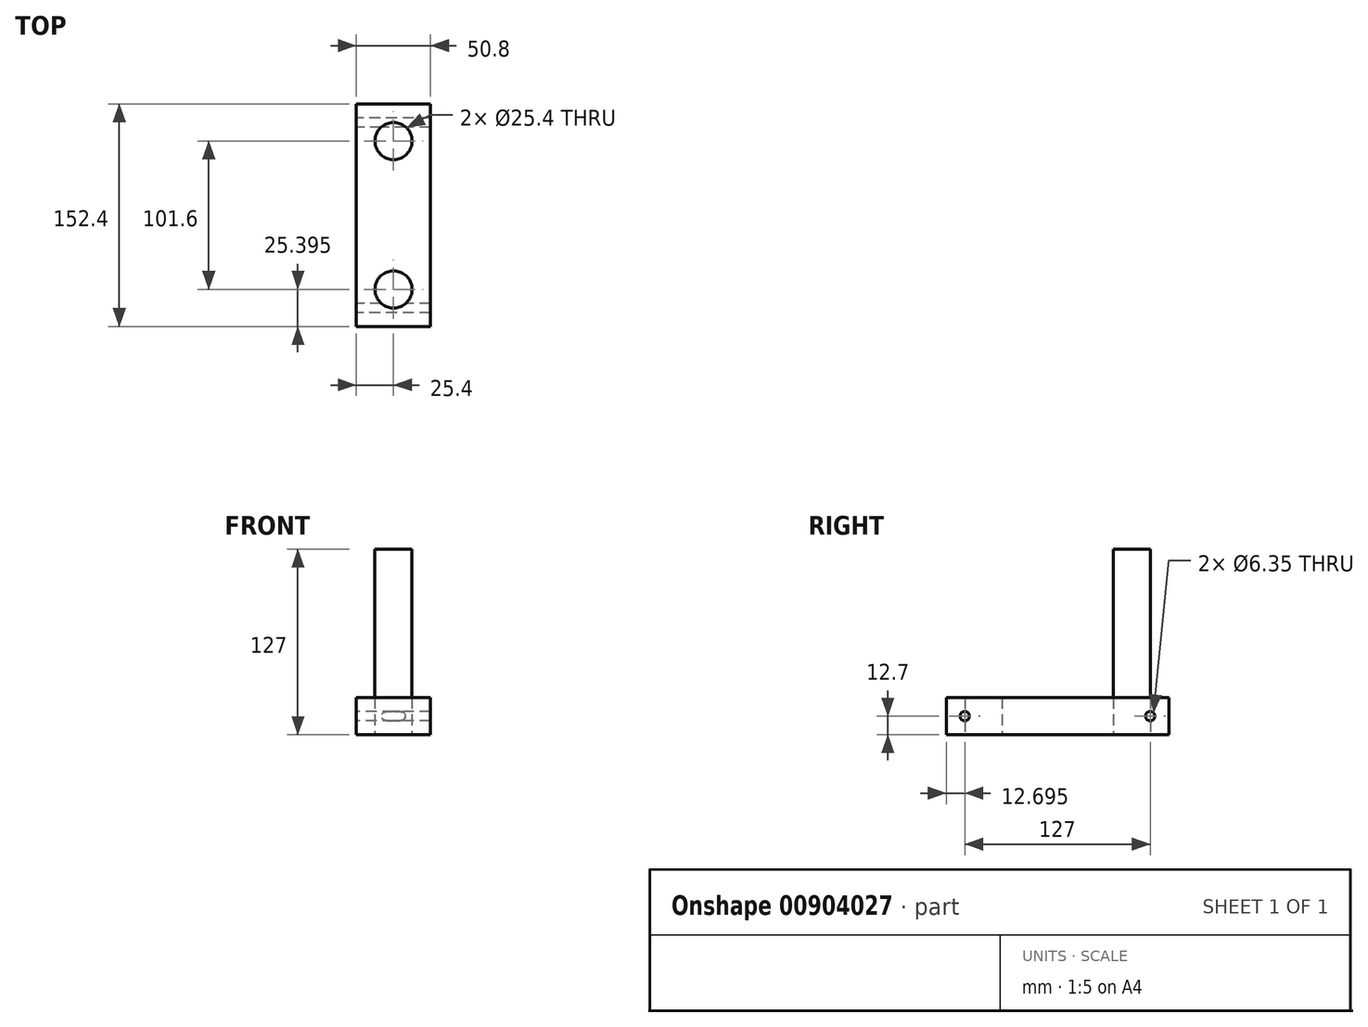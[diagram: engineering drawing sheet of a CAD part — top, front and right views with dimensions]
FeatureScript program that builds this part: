
annotation { "Feature Type Name" : "Feature", "Feature Type Description" : "" }
export const myFeature = defineFeature(function(context is Context, id is Id, definition is map)
    precondition{}
    {
        {
            var Q0;
            Q0=qCreatedBy(makeId("Top.planeOp"),FACE);
            var sketch = newSketch(context, id + "F0", { "sketchPlane" : qUnion([Q0])});
            skLineSegment(sketch, "E0.bottom", {"start": v(-50.8, -51.7) * mm, "end": v(0, -51.7) * mm});
            skLineSegment(sketch, "E0.top", {"start": v(-50.8, 100.7) * mm, "end": v(0, 100.7) * mm});
            skLineSegment(sketch, "E0.left", {"start": v(-50.8, -51.7) * mm, "end": v(-50.8, 100.7) * mm});
            skLineSegment(sketch, "E0.right", {"start": v(0, -51.7) * mm, "end": v(0, 100.7) * mm});
            skLineSegment(sketch, "E1", {"start": v(-25.4, -51.7) * mm, "end": v(-25.4, 100.7) * mm, "construction": true});
            skPoint(sketch, "E2", {"position": v(-25.4, 75.3) * mm});
            skPoint(sketch, "E3", {"position": v(-25.4, -26.3) * mm});
            skCircle(sketch, "E4", {"center": v(-25.4, 75.3) * mm, "radius": 12.7 * mm});
            skCircle(sketch, "E5", {"center": v(-25.4, -26.3) * mm, "radius": 12.7 * mm});
            skSolve(sketch);
        }
        {
            var Q0;
            Q0=makeQuery(id+"F0.imprint","IMPRINT",FACE,{"disambiguationData":[TD([[makeQuery(id+"F0.imprint","IMPRINT",EDGE,{"derivedFrom":sQuery(id+"F0.wireOp",EDGE,"E4")}),1.0]])]});
            extrude(context, id + "F1", {"entities" : qUnion([Q0]), "depth" : 127 * mm, "offsetDistance" : 25.4 * mm});
        }
        {
            var Q0;
            Q0=makeQuery(id+"F0.imprint","IMPRINT",FACE,{"disambiguationData":[TD([[makeQuery(id+"F0.imprint","IMPRINT",EDGE,{"derivedFrom":sQuery(id+"F0.wireOp",EDGE,"E0.bottom")}),1.0]])]});
            extrude(context, id + "F2", {"entities" : qUnion([Q0]), "depth" : 25.4 * mm, "offsetDistance" : 25.4 * mm});
        }
        {
            var Q0;
            Q0=makeQuery(id+"F2.opExtrude","SWEPT_FACE",FACE,{"disambiguationData":[OSD([sQuery(id+"F0.wireOp",EDGE,"E0.left")])]});
            var sketch = newSketch(context, id + "F3", { "sketchPlane" : qUnion([Q0])});
            skLineSegment(sketch, "E6.0", {"start": v(-88, 25.4) * mm, "end": v(-62.6, 25.4) * mm});
            skPoint(sketch, "E7", {"position": v(-88, 25.4) * mm});
            skLineSegment(sketch, "E8.0", {"start": v(13.6, 25.4) * mm, "end": v(39, 25.4) * mm});
            skPoint(sketch, "E9", {"position": v(39, 25.4) * mm});
            skLineSegment(sketch, "E10", {"start": v(-100.7, 12.7) * mm, "end": v(51.7, 12.7) * mm, "construction": true});
            skLineSegment(sketch, "E11", {"start": v(-88, 25.4) * mm, "end": v(-88, 0) * mm, "construction": true});
            skLineSegment(sketch, "E12", {"start": v(39, 25.4) * mm, "end": v(39, 0) * mm, "construction": true});
            skCircle(sketch, "E13", {"center": v(-88, 12.7) * mm, "radius": 3.18 * mm});
            skCircle(sketch, "E14", {"center": v(39, 12.7) * mm, "radius": 3.18 * mm});
            skSolve(sketch);
        }
        {
            var Q0;
            Q0=makeQuery(id+"F3.imprint","IMPRINT",FACE,{"disambiguationData":[TD([[makeQuery(id+"F3.imprint","IMPRINT",EDGE,{"derivedFrom":sQuery(id+"F3.wireOp",EDGE,"E13")}),1.0]])]});
            var Q1;
            Q1=makeQuery(id+"F3.imprint","IMPRINT",FACE,{"disambiguationData":[TD([[makeQuery(id+"F3.imprint","IMPRINT",EDGE,{"derivedFrom":sQuery(id+"F3.wireOp",EDGE,"E14")}),1.0]])]});
            extrude(context, id + "F4", {"entities" : qUnion([Q0, Q1]), "operationType" : NewBodyOperationType.REMOVE, "endBound" : BoundingType.THROUGH_ALL, "oppositeDirection" : true, "depth" : 25.4 * mm, "offsetDistance" : 25.4 * mm});
        }
    });
